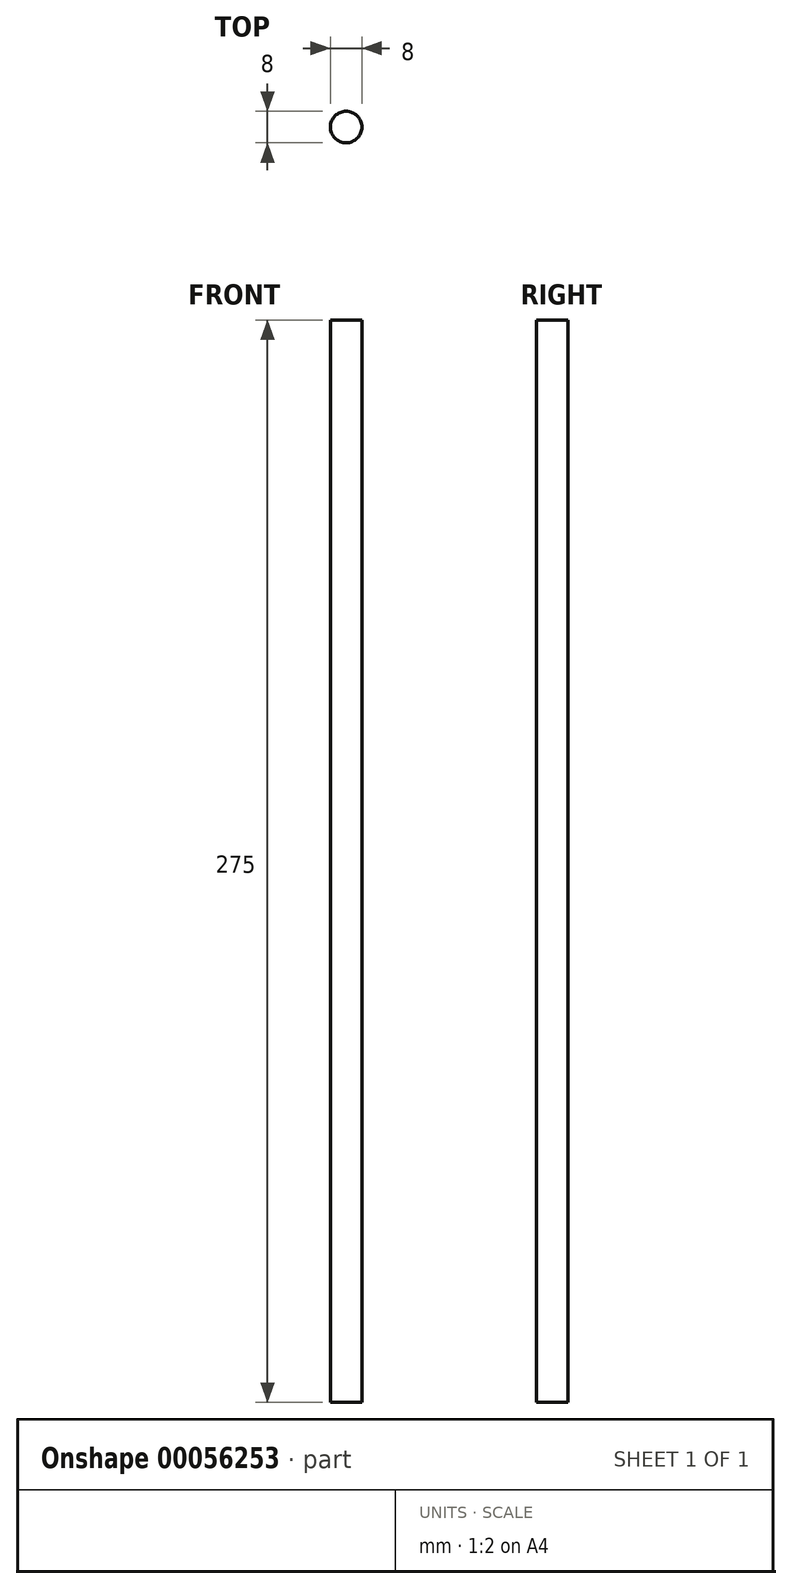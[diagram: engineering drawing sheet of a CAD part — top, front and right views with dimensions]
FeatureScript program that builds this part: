
annotation { "Feature Type Name" : "Feature", "Feature Type Description" : "" }
export const myFeature = defineFeature(function(context is Context, id is Id, definition is map)
    precondition{}
    {
        {
            var Q0;
            Q0=qCreatedBy(makeId("Top.planeOp"),FACE);
            var sketch = newSketch(context, id + "F0", { "sketchPlane" : qUnion([Q0])});
            skCircle(sketch, "E0", {"center": v(0, 0) * mm, "radius": 4 * mm});
            skSolve(sketch);
        }
        {
            var Q0;
            Q0=qSketchRegion(id+"F0",true);
            extrude(context, id + "F1", {"entities" : qUnion([Q0]), "depth" : 275 * mm});
        }
    });
